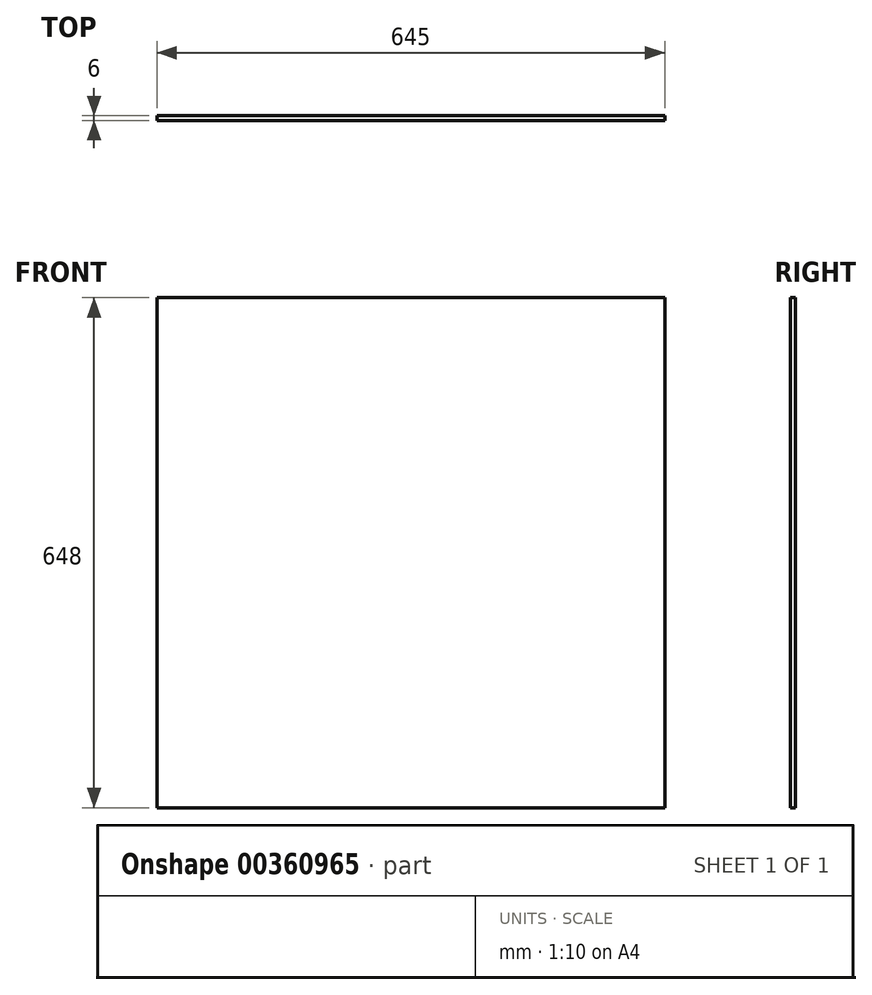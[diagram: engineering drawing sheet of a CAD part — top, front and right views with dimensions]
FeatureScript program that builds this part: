
annotation { "Feature Type Name" : "Feature", "Feature Type Description" : "" }
export const myFeature = defineFeature(function(context is Context, id is Id, definition is map)
    precondition{}
    {
        {
            var Q0;
            Q0=qCreatedBy(makeId("Front.planeOp"),FACE);
            var sketch = newSketch(context, id + "F0", { "sketchPlane" : qUnion([Q0])});
            skLineSegment(sketch, "E0.bottom", {"start": v(322.5, 324) * mm, "end": v(-322.5, 324) * mm});
            skLineSegment(sketch, "E0.top", {"start": v(322.5, -324) * mm, "end": v(-322.5, -324) * mm});
            skLineSegment(sketch, "E0.left", {"start": v(322.5, 324) * mm, "end": v(322.5, -324) * mm});
            skLineSegment(sketch, "E0.right", {"start": v(-322.5, 324) * mm, "end": v(-322.5, -324) * mm});
            skPoint(sketch, "E0.middle", {"position": v(0, 0) * mm});
            skSolve(sketch);
        }
        {
            var Q0;
            Q0=makeQuery(id+"F0.imprint","IMPRINT",FACE,{"disambiguationData":[TD([[makeQuery(id+"F0.imprint","IMPRINT",EDGE,{"derivedFrom":sQuery(id+"F0.wireOp",EDGE,"E0.bottom")}),1.0]])]});
            extrude(context, id + "F1", {"entities" : qUnion([Q0]), "oppositeDirection" : true, "depth" : 6 * mm});
        }
    });
